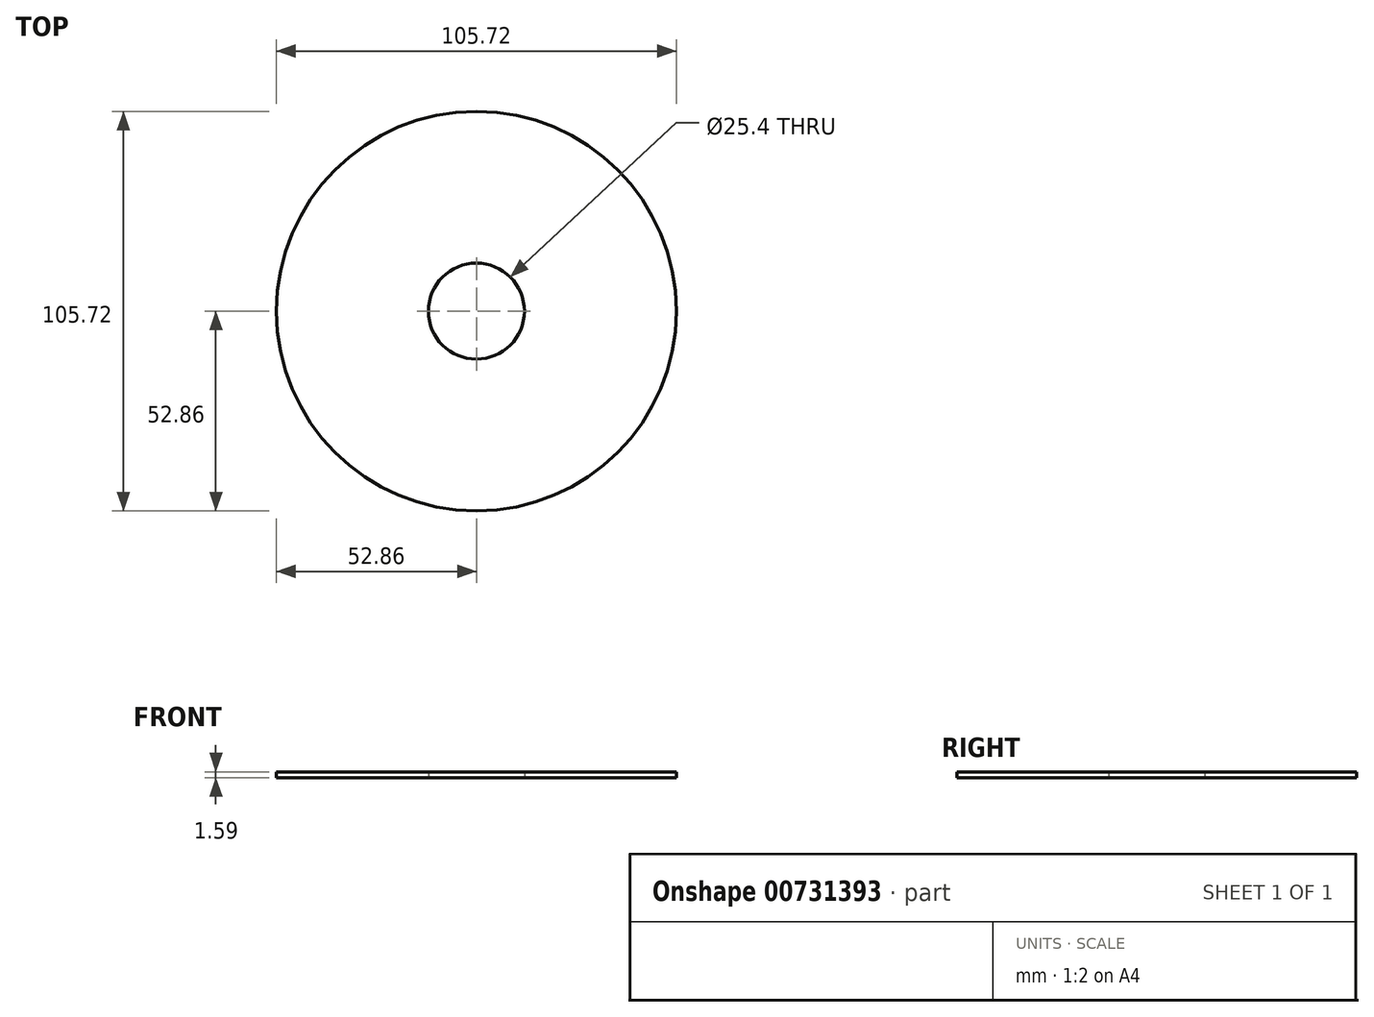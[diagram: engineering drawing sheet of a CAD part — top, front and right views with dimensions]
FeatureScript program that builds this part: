
annotation { "Feature Type Name" : "Feature", "Feature Type Description" : "" }
export const myFeature = defineFeature(function(context is Context, id is Id, definition is map)
    precondition{}
    {
        {
            var Q0;
            Q0=qCreatedBy(makeId("Top.planeOp"),FACE);
            var sketch = newSketch(context, id + "F0", { "sketchPlane" : qUnion([Q0])});
            skCircle(sketch, "E0", {"center": v(0, 0) * mm, "radius": 12.7 * mm});
            skCircle(sketch, "E1", {"center": v(0, 0) * mm, "radius": 52.86 * mm});
            skSolve(sketch);
        }
        {
            var Q0;
            Q0 = qSketchRegion(id + "F0", true);
            extrude(context, id + "F1", {"entities" : qUnion([Q0]), "depth" : 1.59 * mm, "offsetDistance" : 25.4 * mm});
        }
    });
